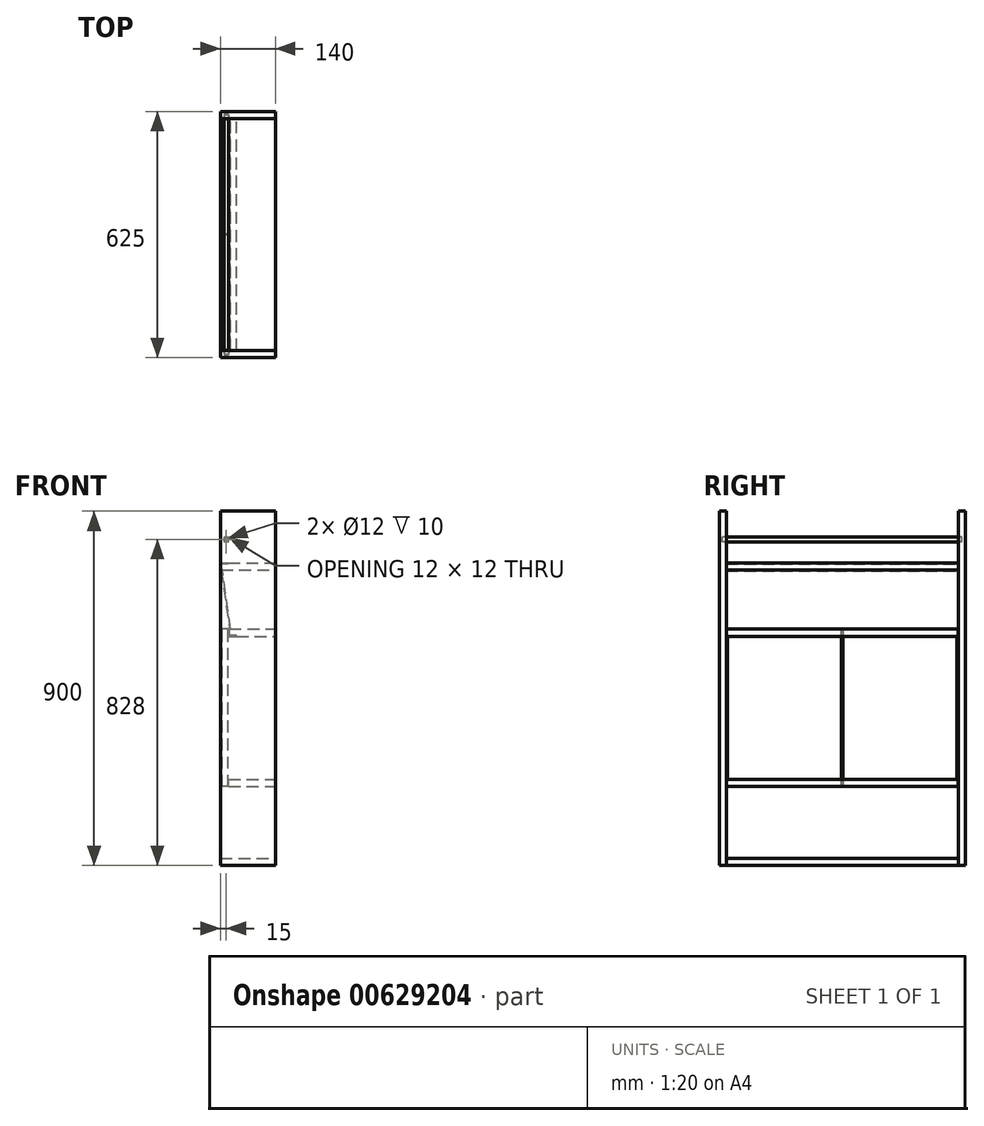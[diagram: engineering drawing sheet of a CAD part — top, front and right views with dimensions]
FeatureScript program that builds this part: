
annotation { "Feature Type Name" : "Feature", "Feature Type Description" : "" }
export const myFeature = defineFeature(function(context is Context, id is Id, definition is map)
    precondition{}
    {
        {
            var Q0;
            Q0=qCreatedBy(makeId("Front.planeOp"),FACE);
            var sketch = newSketch(context, id + "F0", { "sketchPlane" : qUnion([Q0])});
            skLineSegment(sketch, "E0.bottom", {"start": v(0, 0) * mm, "end": v(140, 0) * mm});
            skLineSegment(sketch, "E0.top", {"start": v(0, 18) * mm, "end": v(140, 18) * mm});
            skLineSegment(sketch, "E0.left", {"start": v(0, 0) * mm, "end": v(0, 18) * mm});
            skLineSegment(sketch, "E0.right", {"start": v(140, 0) * mm, "end": v(140, 18) * mm});
            skSolve(sketch);
        }
        {
            var Q0;
            Q0 = qSketchRegion(id + "F0", true);
            extrude(context, id + "F1", {"entities" : qUnion([Q0]), "depth" : 589 * mm, "offsetDistance" : 25 * mm});
        }
        {
            var Q0;
            Q0=qCreatedBy(makeId("Top.planeOp"),FACE);
            var sketch = newSketch(context, id + "F2", { "sketchPlane" : qUnion([Q0])});
            skLineSegment(sketch, "E1.bottom", {"start": v(0, 0) * mm, "end": v(140, 0) * mm});
            skLineSegment(sketch, "E1.top", {"start": v(0, 18) * mm, "end": v(140, 18) * mm});
            skLineSegment(sketch, "E1.left", {"start": v(0, 0) * mm, "end": v(0, 18) * mm});
            skLineSegment(sketch, "E1.right", {"start": v(140, 0) * mm, "end": v(140, 18) * mm});
            skLineSegment(sketch, "E2.bottom", {"start": v(0, -589) * mm, "end": v(140, -589) * mm});
            skLineSegment(sketch, "E2.top", {"start": v(0, -607) * mm, "end": v(140, -607) * mm});
            skLineSegment(sketch, "E2.left", {"start": v(0, -589) * mm, "end": v(0, -607) * mm});
            skLineSegment(sketch, "E2.right", {"start": v(140, -589) * mm, "end": v(140, -607) * mm});
            skSolve(sketch);
        }
        {
            var Q0;
            Q0=makeQuery(id+"F2.imprint","IMPRINT",FACE,{"disambiguationData":[TD([[makeQuery(id+"F2.imprint","IMPRINT",EDGE,{"derivedFrom":sQuery(id+"F2.wireOp",EDGE,"E1.bottom")}),1.0]])]});
            var Q1;
            Q1=makeQuery(id+"F2.imprint","IMPRINT",FACE,{"disambiguationData":[TD([[makeQuery(id+"F2.imprint","IMPRINT",EDGE,{"derivedFrom":sQuery(id+"F2.wireOp",EDGE,"E2.bottom")}),-1.0]])]});
            extrude(context, id + "F3", {"entities" : qUnion([Q0, Q1]), "depth" : 900 * mm, "offsetDistance" : 25 * mm});
        }
        {
            var Q0;
            Q0=makeQuery(id+"F3.opExtrude","SWEPT_FACE",FACE,{"disambiguationData":[OSD([sQuery(id+"F2.wireOp",EDGE,"E1.bottom")])]});
            var sketch = newSketch(context, id + "F4", { "sketchPlane" : qUnion([Q0])});
            skLineSegment(sketch, "E3.bottom", {"start": v(140, 218) * mm, "end": v(21, 218) * mm});
            skLineSegment(sketch, "E3.top", {"start": v(140, 200) * mm, "end": v(21, 200) * mm});
            skLineSegment(sketch, "E3.left", {"start": v(140, 218) * mm, "end": v(140, 200) * mm});
            skLineSegment(sketch, "E3.right", {"start": v(21, 218) * mm, "end": v(21, 200) * mm});
            skLineSegment(sketch, "E4.bottom", {"start": v(140, 600) * mm, "end": v(31, 600) * mm});
            skLineSegment(sketch, "E4.top", {"start": v(140, 582) * mm, "end": v(21, 582) * mm});
            skLineSegment(sketch, "E4.left", {"start": v(140, 600) * mm, "end": v(140, 582) * mm});
            skLineSegment(sketch, "E4.right", {"start": v(21, 600) * mm, "end": v(21, 582) * mm});
            skLineSegment(sketch, "E5.top", {"start": v(26, 595) * mm, "end": v(31, 595) * mm, "construction": true});
            skLineSegment(sketch, "E5.left", {"start": v(26, 600) * mm, "end": v(26, 595) * mm, "construction": true});
            skLineSegment(sketch, "E5.right", {"start": v(31, 600) * mm, "end": v(31, 595) * mm, "construction": true});
            skLineSegment(sketch, "E6.bottom", {"start": v(140, 768) * mm, "end": v(0, 768) * mm});
            skLineSegment(sketch, "E6.top", {"start": v(140, 750) * mm, "end": v(31, 750) * mm});
            skLineSegment(sketch, "E6.left", {"start": v(140, 768) * mm, "end": v(140, 750) * mm});
            skLineSegment(sketch, "E6.right", {"start": v(0, 768) * mm, "end": v(0, 750) * mm});
            skLineSegment(sketch, "E7.top", {"start": v(26, 755) * mm, "end": v(31, 755) * mm, "construction": true});
            skLineSegment(sketch, "E7.left", {"start": v(26, 750) * mm, "end": v(26, 755) * mm, "construction": true});
            skLineSegment(sketch, "E7.right", {"start": v(31, 750) * mm, "end": v(31, 755) * mm, "construction": true});
            skLineSegment(sketch, "E8.trimOffspring", {"start": v(26, 750) * mm, "end": v(0, 750) * mm});
            skLineSegment(sketch, "E9.trimOffspring", {"start": v(26, 600) * mm, "end": v(21, 600) * mm});
            skLineSegment(sketch, "E10", {"start": v(26, 600) * mm, "end": v(31, 600) * mm});
            skLineSegment(sketch, "E11", {"start": v(26, 750) * mm, "end": v(31, 750) * mm});
            skSolve(sketch);
        }
        {
            var Q0;
            Q0 = qSketchRegion(id + "F4", true);
            extrude(context, id + "F5", {"entities" : qUnion([Q0]), "endBound" : BoundingType.UP_TO_NEXT, "depth" : 25 * mm, "offsetDistance" : 25 * mm});
        }
        {
            var Q0;
            Q0=makeQuery(id+"F3.opExtrude","SWEPT_FACE",FACE,{"disambiguationData":[OSD([sQuery(id+"F2.wireOp",EDGE,"E1.bottom")])]});
            var sketch = newSketch(context, id + "F6", { "sketchPlane" : qUnion([Q0])});
            skLineSegment(sketch, "E12", {"start": v(0, 768) * mm, "end": v(0, 748) * mm});
            skLineSegment(sketch, "E13", {"start": v(0, 748) * mm, "end": v(2, 748) * mm});
            skLineSegment(sketch, "E14", {"start": v(2, 748) * mm, "end": v(2, 766) * mm});
            skLineSegment(sketch, "E15", {"start": v(2, 766) * mm, "end": v(20, 766) * mm});
            skLineSegment(sketch, "E16", {"start": v(20, 766) * mm, "end": v(20, 768) * mm});
            skLineSegment(sketch, "E17", {"start": v(20, 768) * mm, "end": v(0, 768) * mm});
            skLineSegment(sketch, "E18", {"start": v(21, 582) * mm, "end": v(21, 602) * mm});
            skLineSegment(sketch, "E19", {"start": v(21, 602) * mm, "end": v(23, 602) * mm});
            skLineSegment(sketch, "E20", {"start": v(23, 602) * mm, "end": v(23, 584) * mm});
            skLineSegment(sketch, "E21", {"start": v(23, 584) * mm, "end": v(41, 584) * mm});
            skLineSegment(sketch, "E22", {"start": v(41, 584) * mm, "end": v(41, 582) * mm});
            skLineSegment(sketch, "E23", {"start": v(41, 582) * mm, "end": v(21, 582) * mm});
            skSolve(sketch);
        }
        {
            var Q0;
            Q0=makeQuery(id+"F6.imprint","IMPRINT",FACE,{"disambiguationData":[TD([[makeQuery(id+"F6.imprint","IMPRINT",EDGE,{"derivedFrom":sQuery(id+"F6.wireOp",EDGE,"E18")}),-1.0]])]});
            var Q1;
            Q1=makeQuery(id+"F6.imprint","IMPRINT",FACE,{"disambiguationData":[TD([[makeQuery(id+"F6.imprint","IMPRINT",EDGE,{"derivedFrom":sQuery(id+"F6.wireOp",EDGE,"E12")}),1.0]])]});
            var Q2;
            Q2=makeQuery(id+"F3.opExtrude","SWEPT_FACE",FACE,{"disambiguationData":[OSD([sQuery(id+"F2.wireOp",EDGE,"E2.bottom")])]});
            var Q3;
            Q3=makeQuery(id+"F3.opExtrude","SWEPT_BODY",BODY,{"disambiguationData":[OSD([sQuery(id+"F2.wireOp",EDGE,"E2.bottom"),sQuery(id+"F2.wireOp",EDGE,"E2.top"),sQuery(id+"F2.wireOp",EDGE,"E2.left"),sQuery(id+"F2.wireOp",EDGE,"E2.right")])]});
            extrude(context, id + "F7", {"entities" : qUnion([Q0, Q1]), "operationType" : NewBodyOperationType.REMOVE, "endBound" : BoundingType.UP_TO_SURFACE, "depth" : 600 * mm, "endBoundEntityFace" : qUnion([Q2]), "endBoundEntityBody" : qUnion([Q3]), "offsetDistance" : 25 * mm});
        }
        {
            var Q0;
            {var subQ1=sQuery(id+"F6.wireOp",EDGE,"E13");Q0=makeQuery(id+"F6.imprint","IMPRINT",FACE,{"disambiguationData":[TD([[makeQuery(id+"F6.imprint","IMPRINT",EDGE,{"derivedFrom":subQ1}),-1.0]])]});}
            var sketch = newSketch(context, id + "F8", { "sketchPlane" : qUnion([Q0])});
            skLineSegment(sketch, "E24.0", {"start": v(20, 768) * mm, "end": v(0, 768) * mm});
            skLineSegment(sketch, "E25.0", {"start": v(20, 766) * mm, "end": v(20, 768) * mm});
            skLineSegment(sketch, "E26.0", {"start": v(2, 766) * mm, "end": v(20, 766) * mm});
            skLineSegment(sketch, "E27.0", {"start": v(2, 748) * mm, "end": v(2, 766) * mm});
            skLineSegment(sketch, "E28.0", {"start": v(0, 748) * mm, "end": v(2, 748) * mm});
            skLineSegment(sketch, "E29.0", {"start": v(0, 768) * mm, "end": v(0, 748) * mm});
            skLineSegment(sketch, "E30.0", {"start": v(21, 582) * mm, "end": v(21, 602) * mm});
            skPoint(sketch, "E31.0", {"position": v(23, 602) * mm});
            skLineSegment(sketch, "E32.0", {"start": v(23, 602) * mm, "end": v(23, 584) * mm});
            skLineSegment(sketch, "E33.0", {"start": v(21, 602) * mm, "end": v(23, 602) * mm});
            skLineSegment(sketch, "E34.0", {"start": v(23, 584) * mm, "end": v(41, 584) * mm});
            skLineSegment(sketch, "E35.0", {"start": v(41, 582) * mm, "end": v(21, 582) * mm});
            skLineSegment(sketch, "E36.0", {"start": v(41, 584) * mm, "end": v(41, 582) * mm});
            skSolve(sketch);
        }
        {
            var Q0;
            Q0=makeQuery(id+"F8.imprint","IMPRINT",FACE,{"disambiguationData":[TD([[makeQuery(id+"F8.imprint","IMPRINT",EDGE,{"derivedFrom":sQuery(id+"F8.wireOp",EDGE,"E30.0")}),-1.0]])]});
            var Q1;
            Q1=makeQuery(id+"F8.imprint","IMPRINT",FACE,{"disambiguationData":[TD([[makeQuery(id+"F8.imprint","IMPRINT",EDGE,{"derivedFrom":sQuery(id+"F8.wireOp",EDGE,"E24.0")}),1.0]])]});
            var Q2;
            Q2=makeQuery(id+"F3.opExtrude","SWEPT_FACE",FACE,{"disambiguationData":[OSD([sQuery(id+"F2.wireOp",EDGE,"E2.bottom")])]});
            extrude(context, id + "F9", {"entities" : qUnion([Q0, Q1]), "endBound" : BoundingType.UP_TO_SURFACE, "depth" : 25 * mm, "endBoundEntityFace" : qUnion([Q2]), "offsetDistance" : 25 * mm});
        }
        {
            var Q0;
            Q0=makeQuery(id+"F3.opExtrude","SWEPT_FACE",FACE,{"disambiguationData":[OSD([sQuery(id+"F2.wireOp",EDGE,"E1.bottom")])]});
            var sketch = newSketch(context, id + "F10", { "sketchPlane" : qUnion([Q0])});
            skLineSegment(sketch, "E37", {"start": v(2, 750) * mm, "end": v(5.03, 750) * mm});
            skLineSegment(sketch, "E38", {"start": v(5.03, 750) * mm, "end": v(26.31, 600) * mm});
            skLineSegment(sketch, "E39", {"start": v(26.31, 600) * mm, "end": v(23.28, 600) * mm});
            skLineSegment(sketch, "E40", {"start": v(23.28, 600) * mm, "end": v(2, 750) * mm});
            skSolve(sketch);
        }
        {
            var Q0;
            Q0 = qSketchRegion(id + "F10", true);
            var Q1;
            Q1=makeQuery(id+"F3.opExtrude","SWEPT_FACE",FACE,{"disambiguationData":[OSD([sQuery(id+"F2.wireOp",EDGE,"E2.bottom")])]});
            extrude(context, id + "F11", {"entities" : qUnion([Q0]), "endBound" : BoundingType.UP_TO_SURFACE, "depth" : 25 * mm, "endBoundEntityFace" : qUnion([Q1]), "offsetDistance" : 25 * mm});
        }
        {
            var Q0;
            Q0=makeQuery(id+"F3.opExtrude","SWEPT_FACE",FACE,{"disambiguationData":[OSD([sQuery(id+"F2.wireOp",EDGE,"E1.bottom")])]});
            var sketch = newSketch(context, id + "F12", { "sketchPlane" : qUnion([Q0])});
            skCircle(sketch, "E41", {"center": v(15, 828) * mm, "radius": 6 * mm});
            skSolve(sketch);
        }
        {
            var Q0;
            Q0 = qSketchRegion(id + "F12", true);
            extrude(context, id + "F13", {"entities" : qUnion([Q0]), "operationType" : NewBodyOperationType.REMOVE, "oppositeDirection" : true, "depth" : 10 * mm, "offsetDistance" : 25 * mm, "hasSecondDirection" : true, "secondDirectionOppositeDirection" : false, "secondDirectionDepth" : 599 * mm});
        }
        {
            var Q0;
            Q0=makeQuery(id+"F13.boolean.opBoolean","COPY",FACE,{"derivedFrom":makeQuery(id+"F13.opExtrude","CAP_FACE",FACE,{"disambiguationData":[OSD([sQuery(id+"F12.wireOp",EDGE,"E41")])],"isStart":false})});
            var sketch = newSketch(context, id + "F14", { "sketchPlane" : qUnion([Q0])});
            skCircle(sketch, "E42.0", {"center": v(15, 828) * mm, "radius": 6 * mm});
            skSolve(sketch);
        }
        {
            var Q0;
            Q0 = qSketchRegion(id + "F14", true);
            var Q1;
            Q1=makeQuery(id+"F13.boolean.opBoolean","COPY",FACE,{"derivedFrom":makeQuery(id+"F13.opExtrude","CAP_FACE",FACE,{"disambiguationData":[OSD([sQuery(id+"F12.wireOp",EDGE,"E41")])],"isStart":true})});
            extrude(context, id + "F15", {"entities" : qUnion([Q0]), "endBound" : BoundingType.UP_TO_SURFACE, "depth" : 25 * mm, "endBoundEntityFace" : qUnion([Q1]), "offsetDistance" : 25 * mm});
        }
        {
            var Q0;
            Q0=makeQuery(id+"F3.opExtrude","SWEPT_FACE",FACE,{"disambiguationData":[OSD([sQuery(id+"F2.wireOp",EDGE,"E1.left")])]});
            var sketch = newSketch(context, id + "F16", { "sketchPlane" : qUnion([Q0])});
            skLineSegment(sketch, "E43.bottom", {"start": v(586, 200) * mm, "end": v(296, 200) * mm});
            skLineSegment(sketch, "E43.top", {"start": v(586, 600) * mm, "end": v(296, 600) * mm});
            skLineSegment(sketch, "E43.left", {"start": v(586, 200) * mm, "end": v(586, 600) * mm});
            skLineSegment(sketch, "E43.right", {"start": v(296, 200) * mm, "end": v(296, 600) * mm});
            skLineSegment(sketch, "E44.bottom", {"start": v(3, 600) * mm, "end": v(293, 600) * mm});
            skLineSegment(sketch, "E44.top", {"start": v(3, 200) * mm, "end": v(293, 200) * mm});
            skLineSegment(sketch, "E44.left", {"start": v(3, 600) * mm, "end": v(3, 200) * mm});
            skLineSegment(sketch, "E44.right", {"start": v(293, 600) * mm, "end": v(293, 200) * mm});
            skSolve(sketch);
        }
        {
            var Q0;
            Q0 = qSketchRegion(id + "F16", true);
            extrude(context, id + "F17", {"entities" : qUnion([Q0]), "oppositeDirection" : true, "depth" : 4 * mm, "offsetDistance" : 25 * mm});
        }
        {
            var Q0;
            Q0=makeQuery(id+"F17.opExtrude","CAP_FACE",FACE,{"disambiguationData":[OSD([sQuery(id+"F16.wireOp",EDGE,"E43.bottom"),sQuery(id+"F16.wireOp",EDGE,"E43.top"),sQuery(id+"F16.wireOp",EDGE,"E43.left"),sQuery(id+"F16.wireOp",EDGE,"E43.right")])],"isStart":false});
            var sketch = newSketch(context, id + "F18", { "sketchPlane" : qUnion([Q0])});
            skLineSegment(sketch, "E45.0", {"start": v(-586, 600) * mm, "end": v(-296, 600) * mm});
            skLineSegment(sketch, "E46.0", {"start": v(-296, 200) * mm, "end": v(-296, 600) * mm});
            skLineSegment(sketch, "E47.0", {"start": v(-293, 600) * mm, "end": v(-293, 200) * mm});
            skLineSegment(sketch, "E48.0", {"start": v(-3, 600) * mm, "end": v(-293, 600) * mm});
            skLineSegment(sketch, "E49.0", {"start": v(-586, 200) * mm, "end": v(-586, 600) * mm});
            skLineSegment(sketch, "E50.0", {"start": v(-3, 600) * mm, "end": v(-3, 200) * mm});
            skLineSegment(sketch, "E51.0", {"start": v(-3, 200) * mm, "end": v(-293, 200) * mm});
            skLineSegment(sketch, "E52.0", {"start": v(-586, 200) * mm, "end": v(-296, 200) * mm});
            skSolve(sketch);
        }
        {
            var Q0;
            Q0 = qSketchRegion(id + "F18", true);
            extrude(context, id + "F19", {"entities" : qUnion([Q0]), "depth" : 16 * mm, "offsetDistance" : 25 * mm});
        }
    });
